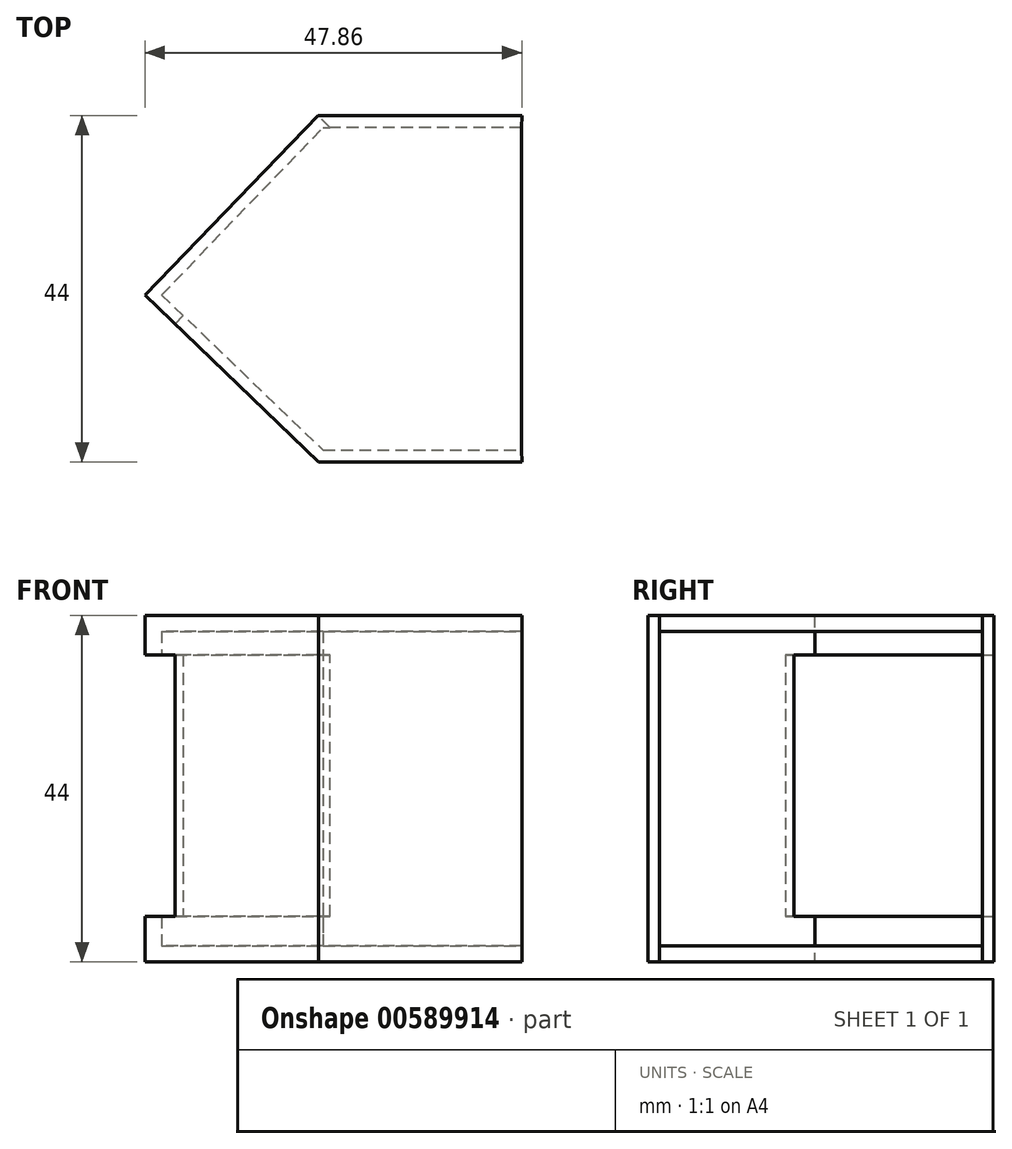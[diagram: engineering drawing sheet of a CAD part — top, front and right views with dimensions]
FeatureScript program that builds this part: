
annotation { "Feature Type Name" : "Feature", "Feature Type Description" : "" }
export const myFeature = defineFeature(function(context is Context, id is Id, definition is map)
    precondition{}
    {
        {
            var Q0;
            Q0=qCreatedBy(makeId("Top.planeOp"),FACE);
            var sketch = newSketch(context, id + "F0", { "sketchPlane" : qUnion([Q0])});
            skLineSegment(sketch, "E0.0", {"start": v(-24.5, 20.57) * mm, "end": v(-13.5, 20.57) * mm});
            skLineSegment(sketch, "E0.1", {"start": v(-13.5, -23.43) * mm, "end": v(-39.34, -23.43) * mm});
            skLineSegment(sketch, "E0.2", {"start": v(-39.34, -23.43) * mm, "end": v(-61.35, -2.25) * mm});
            skLineSegment(sketch, "E0.3", {"start": v(-39.38, 20.57) * mm, "end": v(-61.35, -2.25) * mm});
            skLineSegment(sketch, "E0.4", {"start": v(-24.5, 20.57) * mm, "end": v(-39.38, 20.57) * mm});
            skLineSegment(sketch, "E1.0", {"start": v(-13.53, -21.93) * mm, "end": v(-38.73, -21.93) * mm});
            skLineSegment(sketch, "E1.1", {"start": v(-24.53, 19.07) * mm, "end": v(-13.53, 19.07) * mm});
            skLineSegment(sketch, "E1.2", {"start": v(-24.53, 19.07) * mm, "end": v(-38.75, 19.07) * mm});
            skLineSegment(sketch, "E1.3", {"start": v(-38.75, 19.07) * mm, "end": v(-59.22, -2.2) * mm});
            skLineSegment(sketch, "E1.4", {"start": v(-38.73, -21.93) * mm, "end": v(-59.22, -2.2) * mm});
            skLineSegment(sketch, "E2", {"start": v(-13.5, -23.43) * mm, "end": v(-13.53, -21.93) * mm});
            skLineSegment(sketch, "E3", {"start": v(-13.53, 19.07) * mm, "end": v(-13.5, 20.57) * mm});
            skSolve(sketch);
        }
        {
            var Q0;
            Q0 = qSketchRegion(id + "F0", true);
            extrude(context, id + "F1", {"entities" : qUnion([Q0]), "depth" : 40 * mm, "offsetDistance" : 25 * mm});
        }
        {
            var Q0;
            Q0=makeQuery(id+"F1.opExtrude","CAP_FACE",FACE,{"disambiguationData":[OSD([sQuery(id+"F0.wireOp",EDGE,"E0.0"),sQuery(id+"F0.wireOp",EDGE,"E0.1"),sQuery(id+"F0.wireOp",EDGE,"E0.2"),sQuery(id+"F0.wireOp",EDGE,"E0.3"),sQuery(id+"F0.wireOp",EDGE,"E0.4"),sQuery(id+"F0.wireOp",EDGE,"E1.0"),sQuery(id+"F0.wireOp",EDGE,"E1.1"),sQuery(id+"F0.wireOp",EDGE,"E1.2"),sQuery(id+"F0.wireOp",EDGE,"E1.3"),sQuery(id+"F0.wireOp",EDGE,"E1.4"),sQuery(id+"F0.wireOp",EDGE,"E2"),sQuery(id+"F0.wireOp",EDGE,"E3")])],"isStart":false});
            extrude(context, id + "F2", {"entities" : qUnion([Q0]), "operationType" : NewBodyOperationType.ADD, "depth" : 2 * mm, "offsetDistance" : 25 * mm});
        }
        {
            var Q0;
            Q0=makeQuery(id+"F2.opExtrude","CAP_FACE",FACE,{"disambiguationData":[OSD([sQuery(id+"F0.wireOp",EDGE,"E0.0"),sQuery(id+"F0.wireOp",EDGE,"E0.1"),sQuery(id+"F0.wireOp",EDGE,"E0.2"),sQuery(id+"F0.wireOp",EDGE,"E0.3"),sQuery(id+"F0.wireOp",EDGE,"E0.4"),sQuery(id+"F0.wireOp",EDGE,"E1.0"),sQuery(id+"F0.wireOp",EDGE,"E1.1"),sQuery(id+"F0.wireOp",EDGE,"E1.2"),sQuery(id+"F0.wireOp",EDGE,"E1.3"),sQuery(id+"F0.wireOp",EDGE,"E1.4"),sQuery(id+"F0.wireOp",EDGE,"E2"),sQuery(id+"F0.wireOp",EDGE,"E3")])],"isStart":false});
            extrude(context, id + "F3", {"entities" : qUnion([Q0]), "operationType" : NewBodyOperationType.ADD, "depth" : 2 * mm, "offsetDistance" : 25 * mm});
        }
        {
            var Q0;
            {var subQ0=sQuery(id+"F0.wireOp",EDGE,"E1.2");var subQ1=sQuery(id+"F0.wireOp",EDGE,"E1.1");Q0=makeQuery(id+"F3.boolean.opBoolean","MERGE",FACE,{"derivedFrom":[makeQuery(id+"F2.boolean.opBoolean","MERGE",FACE,{"derivedFrom":[makeQuery(id+"F1.opExtrude","SWEPT_FACE",FACE,{"disambiguationData":[OSD([subQ1,subQ0])]}),makeQuery(id+"F2.opExtrude","SWEPT_FACE",FACE,{"disambiguationData":[OSD([subQ1,subQ0])]})]}),makeQuery(id+"F3.opExtrude","SWEPT_FACE",FACE,{"disambiguationData":[OSD([subQ1,subQ0])]})]});}
            var sketch = newSketch(context, id + "F4", { "sketchPlane" : qUnion([Q0])});
            skLineSegment(sketch, "E4", {"start": v(-13.53, 44) * mm, "end": v(-13.53, 42) * mm});
            skLineSegment(sketch, "E5", {"start": v(-13.53, 42) * mm, "end": v(-38.75, 42) * mm});
            skSolve(sketch);
        }
        {
            var Q0;
            Q0=makeQuery(id+"F4.imprint","IMPRINT",FACE,{"disambiguationData":[TD([[makeQuery(id+"F4.imprint","IMPRINT",EDGE,{"derivedFrom":sQuery(id+"F4.wireOp",EDGE,"E4")}),-1.0]])]});
            extrude(context, id + "F5", {"entities" : qUnion([Q0]), "operationType" : NewBodyOperationType.ADD, "depth" : 42.1 * mm, "offsetDistance" : 25 * mm});
        }
        {
            var Q0;
            Q0=makeQuery(id+"F5.opExtrude","SWEPT_FACE",FACE,{"disambiguationData":[OSD([sQuery(id+"F0.wireOp",EDGE,"E1.2"),sQuery(id+"F0.wireOp",EDGE,"E1.3")])]});
            extrude(context, id + "F6", {"entities" : qUnion([Q0]), "operationType" : NewBodyOperationType.ADD, "endBound" : BoundingType.UP_TO_NEXT, "depth" : 25 * mm, "offsetDistance" : 25 * mm});
        }
        {
            var Q0;
            {var subQ0=sQuery(id+"F0.wireOp",EDGE,"E1.2");var subQ1=sQuery(id+"F0.wireOp",EDGE,"E1.1");Q0=makeQuery(id+"F3.boolean.opBoolean","MERGE",FACE,{"derivedFrom":[makeQuery(id+"F2.boolean.opBoolean","MERGE",FACE,{"derivedFrom":[makeQuery(id+"F1.opExtrude","SWEPT_FACE",FACE,{"disambiguationData":[OSD([subQ1,subQ0])]}),makeQuery(id+"F2.opExtrude","SWEPT_FACE",FACE,{"disambiguationData":[OSD([subQ1,subQ0])]})]}),makeQuery(id+"F3.opExtrude","SWEPT_FACE",FACE,{"disambiguationData":[OSD([subQ1,subQ0])]})]});}
            var sketch = newSketch(context, id + "F7", { "sketchPlane" : qUnion([Q0])});
            skLineSegment(sketch, "E6", {"start": v(-13.53, 0) * mm, "end": v(-13.53, 2) * mm});
            skLineSegment(sketch, "E7", {"start": v(-13.53, 2) * mm, "end": v(-46.07, 2) * mm});
            skSolve(sketch);
        }
        {
            var Q0;
            {var subQ0=sQuery(id+"F7.wireOp",EDGE,"E6");Q0=makeQuery(id+"F7.imprint","IMPRINT",FACE,{"disambiguationData":[TD([[makeQuery(id+"F7.imprint","IMPRINT",EDGE,{"derivedFrom":subQ0}),-1.0]])]});}
            extrude(context, id + "F8", {"entities" : qUnion([Q0]), "operationType" : NewBodyOperationType.ADD, "depth" : 42 * mm, "offsetDistance" : 25 * mm});
        }
        {
            var Q0;
            Q0=makeQuery(id+"F8.opExtrude","SWEPT_FACE",FACE,{"disambiguationData":[OSD([sQuery(id+"F0.wireOp",EDGE,"E1.2"),sQuery(id+"F0.wireOp",EDGE,"E1.3")])]});
            extrude(context, id + "F9", {"entities" : qUnion([Q0]), "operationType" : NewBodyOperationType.ADD, "endBound" : BoundingType.UP_TO_NEXT, "depth" : 25 * mm, "offsetDistance" : 25 * mm});
        }
        {
            var Q0;
            {var subQ0=sQuery(id+"F0.wireOp",EDGE,"E0.3");Q0=makeQuery(id+"F3.boolean.opBoolean","MERGE",FACE,{"derivedFrom":[makeQuery(id+"F2.boolean.opBoolean","MERGE",FACE,{"derivedFrom":[makeQuery(id+"F1.opExtrude","SWEPT_FACE",FACE,{"disambiguationData":[OSD([subQ0])]}),makeQuery(id+"F2.opExtrude","SWEPT_FACE",FACE,{"disambiguationData":[OSD([subQ0])]})]}),makeQuery(id+"F3.opExtrude","SWEPT_FACE",FACE,{"disambiguationData":[OSD([subQ0])]})]});}
            var sketch = newSketch(context, id + "F10", { "sketchPlane" : qUnion([Q0])});
            skLineSegment(sketch, "E8", {"start": v(12.5, 44) * mm, "end": v(12.5, 39) * mm});
            skLineSegment(sketch, "E9", {"start": v(12.5, 39) * mm, "end": v(44.16, 39) * mm});
            skLineSegment(sketch, "E10", {"start": v(12.5, 0) * mm, "end": v(12.5, 5.77) * mm});
            skLineSegment(sketch, "E11", {"start": v(12.5, 5.77) * mm, "end": v(44.16, 5.77) * mm});
            skLineSegment(sketch, "E12", {"start": v(44.16, 5.77) * mm, "end": v(39.16, 5.77) * mm});
            skLineSegment(sketch, "E13", {"start": v(39.16, 5.77) * mm, "end": v(39.16, 39) * mm});
            skLineSegment(sketch, "E14", {"start": v(12.5, 5.77) * mm, "end": v(17.5, 5.77) * mm});
            skLineSegment(sketch, "E15", {"start": v(17.5, 5.77) * mm, "end": v(17.5, 39) * mm});
            skSolve(sketch);
        }
        {
            var Q0;
            Q0=makeQuery(id+"F10.imprint","IMPRINT",FACE,{"disambiguationData":[TD([[makeQuery(id+"F10.imprint","IMPRINT",EDGE,{"derivedFrom":sQuery(id+"F10.wireOp",EDGE,"E11")}),1.0]])]});
            extrude(context, id + "F11", {"entities" : qUnion([Q0]), "operationType" : NewBodyOperationType.REMOVE, "oppositeDirection" : true, "depth" : 5.3 * mm, "offsetDistance" : 25 * mm});
        }
    });
